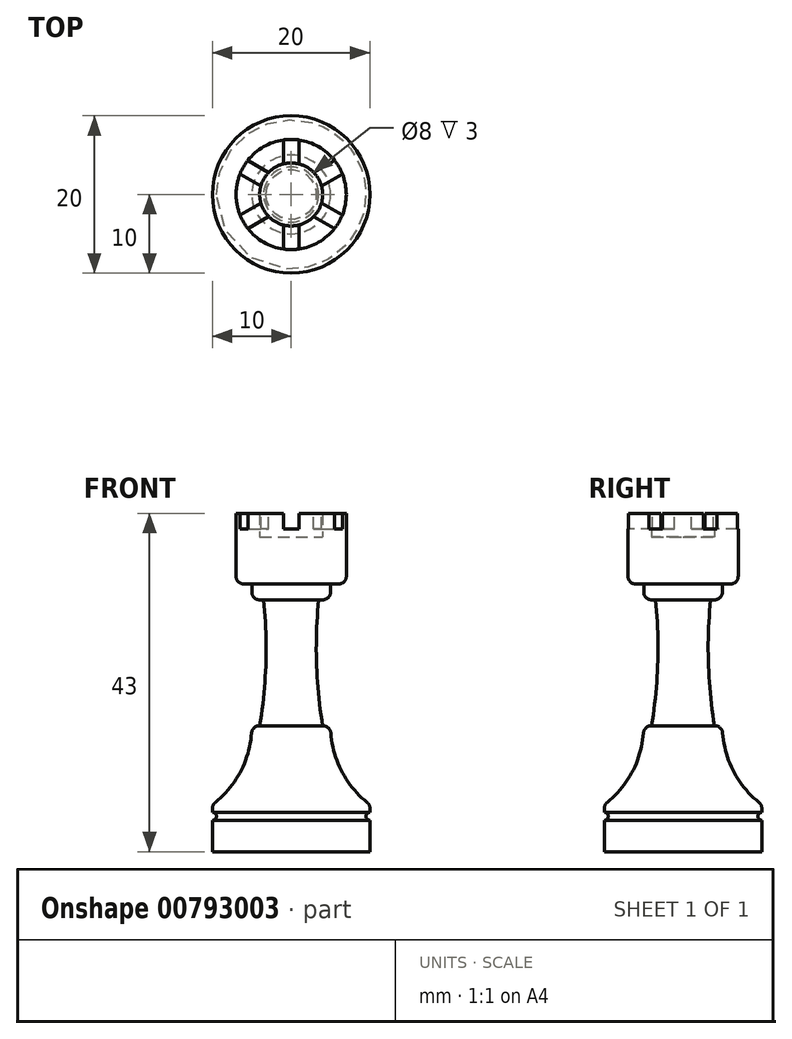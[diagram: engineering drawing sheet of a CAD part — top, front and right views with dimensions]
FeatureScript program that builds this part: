
annotation { "Feature Type Name" : "Feature", "Feature Type Description" : "" }
export const myFeature = defineFeature(function(context is Context, id is Id, definition is map)
    precondition{}
    {
        {
            var Q0;
            Q0=qCreatedBy(makeId("Front.planeOp"),FACE);
            var sketch = newSketch(context, id + "F0", { "sketchPlane" : qUnion([Q0])});
            skLineSegment(sketch, "E0.top", {"start": v(-10, 0) * mm, "end": v(10, 0) * mm, "construction": true});
            skLineSegment(sketch, "E0.left", {"start": v(10, 43) * mm, "end": v(10, 0) * mm, "construction": true});
            skLineSegment(sketch, "E0.right", {"start": v(-10, 43) * mm, "end": v(-10, 0) * mm, "construction": true});
            skLineSegment(sketch, "E1", {"start": v(0, 0) * mm, "end": v(0, 4) * mm, "construction": true});
            skLineSegment(sketch, "E2", {"start": v(0, 4) * mm, "end": v(-10, 4) * mm, "construction": true});
            skLineSegment(sketch, "E3", {"start": v(0, 4) * mm, "end": v(0, 5) * mm, "construction": true});
            skLineSegment(sketch, "E4", {"start": v(0, 5) * mm, "end": v(-10, 5) * mm, "construction": true});
            skLineSegment(sketch, "E5", {"start": v(0, 5) * mm, "end": v(0, 6) * mm, "construction": true});
            skLineSegment(sketch, "E6", {"start": v(0, 6) * mm, "end": v(-10, 6) * mm, "construction": true});
            skLineSegment(sketch, "E7", {"start": v(-9, 5) * mm, "end": v(-9, 4) * mm, "construction": true});
            skLineSegment(sketch, "E8", {"start": v(0, 6) * mm, "end": v(0, 16) * mm, "construction": true});
            skLineSegment(sketch, "E9", {"start": v(0, 16) * mm, "end": v(-10, 16) * mm, "construction": true});
            skLineSegment(sketch, "E10", {"start": v(0, 16) * mm, "end": v(0, 32) * mm, "construction": true});
            skLineSegment(sketch, "E11", {"start": v(0, 32) * mm, "end": v(-10, 32) * mm, "construction": true});
            skLineSegment(sketch, "E12", {"start": v(0, 32) * mm, "end": v(0, 34) * mm, "construction": true});
            skLineSegment(sketch, "E13", {"start": v(0, 34) * mm, "end": v(-10, 34) * mm, "construction": true});
            skLineSegment(sketch, "E14", {"start": v(-5, 16) * mm, "end": v(-5, 6) * mm, "construction": true});
            skLineSegment(sketch, "E15", {"start": v(0, 0) * mm, "end": v(-10, 0) * mm});
            skLineSegment(sketch, "E16", {"start": v(-10, 4) * mm, "end": v(-10, 0) * mm});
            skArc(sketch, "E17", {"start": v(-10, 4) * mm, "mid": v(-9.5, 4.5) * mm, "end": v(-10, 5) * mm});
            skLineSegment(sketch, "E18", {"start": v(-10, 5) * mm, "end": v(-10, 6) * mm});
            skArc(sketch, "E19", {"start": v(-10, 6) * mm, "mid": v(-6.32, 10.4) * mm, "end": v(-5, 16) * mm});
            skLineSegment(sketch, "E20", {"start": v(-5, 16) * mm, "end": v(-4, 16) * mm});
            skPoint(sketch, "E21.snap10", {"position": v(0, 33) * mm});
            skLineSegment(sketch, "E22", {"start": v(0, 0) * mm, "end": v(0, 54.13) * mm, "construction": true});
            skLineSegment(sketch, "E23", {"start": v(0, 43) * mm, "end": v(0, 0) * mm});
            skLineSegment(sketch, "E24", {"start": v(-7, 43) * mm, "end": v(-7, 34) * mm, "construction": true});
            skLineSegment(sketch, "E25", {"start": v(-5, 34) * mm, "end": v(-5, 32) * mm, "construction": true});
            skLineSegment(sketch, "E26", {"start": v(-3.5, 32) * mm, "end": v(-4, 16) * mm, "construction": true});
            skArc(sketch, "E27", {"start": v(-4, 16) * mm, "mid": v(-3.21, 23.98) * mm, "end": v(-3.5, 32) * mm});
            skLineSegment(sketch, "E28", {"start": v(-3.5, 32) * mm, "end": v(-5, 32) * mm});
            skLineSegment(sketch, "E29", {"start": v(-5, 32) * mm, "end": v(-5, 34) * mm});
            skLineSegment(sketch, "E30", {"start": v(-5, 34) * mm, "end": v(-7, 34) * mm});
            skLineSegment(sketch, "E31", {"start": v(-7, 34) * mm, "end": v(-7, 43) * mm});
            skLineSegment(sketch, "E32", {"start": v(-4, 43) * mm, "end": v(-4, 34) * mm, "construction": true});
            skLineSegment(sketch, "E33", {"start": v(-4, 40) * mm, "end": v(0, 40) * mm});
            skLineSegment(sketch, "E34", {"start": v(-4, 40) * mm, "end": v(-4, 43) * mm});
            skLineSegment(sketch, "E35", {"start": v(-7, 43) * mm, "end": v(-4, 43) * mm});
            skSolve(sketch);
        }
        {
            var Q0;
            Q0=qSketchRegion(id+"F0",true);
            var Q1;
            Q1=sQuery(id+"F0.wireOp",EDGE,"E22");
            revolve(context, id + "F1", {"surfaceOperationType" : NewSurfaceOperationType.NEW, "entities" : qUnion([Q0]), "axis" : qUnion([Q1]), "revolveType" : RevolveType.FULL});
        }
        {
            var Q0;
            Q0=makeQuery(id+"F1.opRevolve","SWEPT_EDGE",EDGE,{"disambiguationData":[OSD([sQuery(id+"F0.wireOp",EDGE,"E18"),sQuery(id+"F0.wireOp",EDGE,"E19")])]});
            var Q1;
            Q1=makeQuery(id+"F1.opRevolve","SWEPT_EDGE",EDGE,{"disambiguationData":[OSD([sQuery(id+"F0.wireOp",EDGE,"E19"),sQuery(id+"F0.wireOp",EDGE,"E20")])]});
            fillet(context, id + "F2", {"entities" : qUnion([Q0, Q1]), "radius" : 1 * mm, "tangentPropagation" : true, "allowEdgeOverflow" : false});
        }
        {
            var Q0;
            Q0=makeQuery(id+"F1.opRevolve","SWEPT_EDGE",EDGE,{"disambiguationData":[OSD([sQuery(id+"F0.wireOp",EDGE,"E30"),sQuery(id+"F0.wireOp",EDGE,"E31")])]});
            var Q1;
            Q1=makeQuery(id+"F1.opRevolve","SWEPT_EDGE",EDGE,{"disambiguationData":[OSD([sQuery(id+"F0.wireOp",EDGE,"E28"),sQuery(id+"F0.wireOp",EDGE,"E29")])]});
            fillet(context, id + "F3", {"entities" : qUnion([Q0, Q1]), "radius" : 1 * mm, "tangentPropagation" : true, "allowEdgeOverflow" : false});
        }
        {
            var Q0;
            Q0=makeQuery(id+"F1.opRevolve","SWEPT_FACE",FACE,{"disambiguationData":[OSD([sQuery(id+"F0.wireOp",EDGE,"E35")])]});
            var sketch = newSketch(context, id + "F4", { "sketchPlane" : qUnion([Q0])});
            skLineSegment(sketch, "E36", {"start": v(0, 7) * mm, "end": v(0, 0) * mm, "construction": true});
            skLineSegment(sketch, "E37", {"start": v(-1, 0) * mm, "end": v(-1, 7.52) * mm, "construction": true});
            skLineSegment(sketch, "E38", {"start": v(-1, 7.52) * mm, "end": v(1, 7.52) * mm, "construction": true});
            skLineSegment(sketch, "E39", {"start": v(1, 7.52) * mm, "end": v(1, 0) * mm, "construction": true});
            skLineSegment(sketch, "E40", {"start": v(-1, 6.93) * mm, "end": v(-1, 3.87) * mm});
            skLineSegment(sketch, "E41", {"start": v(1, 6.93) * mm, "end": v(1, 3.87) * mm});
            skLineSegment(sketch, "E42.1.0", {"start": v(-0.5, -0.87) * mm, "end": v(-7, 2.9) * mm, "construction": true});
            skLineSegment(sketch, "E42.1.1", {"start": v(-6.06, 3.5) * mm, "end": v(0, 0) * mm, "construction": true});
            skLineSegment(sketch, "E42.1.2", {"start": v(-6, 4.62) * mm, "end": v(0.5, 0.87) * mm, "construction": true});
            skLineSegment(sketch, "E42.2.0", {"start": v(0.5, -0.87) * mm, "end": v(-6, -4.62) * mm, "construction": true});
            skLineSegment(sketch, "E42.2.1", {"start": v(-6.06, -3.5) * mm, "end": v(0, 0) * mm, "construction": true});
            skLineSegment(sketch, "E42.2.2", {"start": v(-7, -2.9) * mm, "end": v(-0.5, 0.87) * mm, "construction": true});
            skLineSegment(sketch, "E42.3.0", {"start": v(1, 0) * mm, "end": v(1, -7.52) * mm, "construction": true});
            skLineSegment(sketch, "E42.3.1", {"start": v(0, -7) * mm, "end": v(0, 0) * mm, "construction": true});
            skLineSegment(sketch, "E42.3.2", {"start": v(-1, -7.52) * mm, "end": v(-1, 0) * mm, "construction": true});
            skLineSegment(sketch, "E42.4.0", {"start": v(0.5, 0.87) * mm, "end": v(7, -2.9) * mm, "construction": true});
            skLineSegment(sketch, "E42.4.1", {"start": v(6.06, -3.5) * mm, "end": v(0, 0) * mm, "construction": true});
            skLineSegment(sketch, "E42.4.2", {"start": v(6, -4.62) * mm, "end": v(-0.5, -0.87) * mm, "construction": true});
            skLineSegment(sketch, "E42.5.0", {"start": v(-0.5, 0.87) * mm, "end": v(6, 4.62) * mm, "construction": true});
            skLineSegment(sketch, "E42.5.1", {"start": v(6.06, 3.5) * mm, "end": v(0, 0) * mm, "construction": true});
            skLineSegment(sketch, "E42.5.2", {"start": v(7, 2.9) * mm, "end": v(0.5, -0.87) * mm, "construction": true});
            skPoint(sketch, "E42.center", {"position": v(0, 0) * mm});
            skLineSegment(sketch, "E43", {"start": v(-5.5, 4.33) * mm, "end": v(-2.85, 2.8) * mm});
            skLineSegment(sketch, "E44", {"start": v(-6.5, 2.6) * mm, "end": v(-3.85, 1.07) * mm});
            skLineSegment(sketch, "E45", {"start": v(-6.5, -2.6) * mm, "end": v(-3.85, -1.07) * mm});
            skLineSegment(sketch, "E46", {"start": v(-5.5, -4.33) * mm, "end": v(-2.85, -2.8) * mm});
            skLineSegment(sketch, "E47", {"start": v(-1, -3.87) * mm, "end": v(-1, -6.93) * mm});
            skLineSegment(sketch, "E48", {"start": v(1, -3.87) * mm, "end": v(1, -6.93) * mm});
            skLineSegment(sketch, "E49", {"start": v(2.85, -2.8) * mm, "end": v(5.5, -4.33) * mm});
            skLineSegment(sketch, "E50", {"start": v(3.85, -1.07) * mm, "end": v(6.5, -2.6) * mm});
            skLineSegment(sketch, "E51", {"start": v(3.85, 1.07) * mm, "end": v(6.5, 2.6) * mm});
            skLineSegment(sketch, "E52", {"start": v(2.85, 2.8) * mm, "end": v(5.5, 4.33) * mm});
            skSolve(sketch);
        }
        {
            var Q0;
            Q0 = qSketchRegion(id + "F4", true);
            var Q1;
            {var subQ0=sQuery(id+"F4.wireOp",EDGE,"E40");Q1=makeQuery(id+"F4.imprint","IMPRINT",FACE,{"disambiguationData":[TD([[makeQuery(id+"F4.imprint","IMPRINT",EDGE,{"derivedFrom":subQ0}),1.0]])]});}
            extrude(context, id + "F5", {"entities" : qUnion([Q0, Q1]), "operationType" : NewBodyOperationType.REMOVE, "oppositeDirection" : true, "depth" : 2 * mm, "offsetDistance" : 25 * mm});
        }
        {
            var Q0;
            {var subQ0=sQuery(id+"F4.wireOp",EDGE,"E43");Q0=makeQuery(id+"F4.imprint","IMPRINT",FACE,{"disambiguationData":[TD([[makeQuery(id+"F4.imprint","IMPRINT",EDGE,{"derivedFrom":subQ0}),-1.0]])]});}
            var Q1;
            {var subQ0=sQuery(id+"F4.wireOp",EDGE,"E45");Q1=makeQuery(id+"F4.imprint","IMPRINT",FACE,{"disambiguationData":[TD([[makeQuery(id+"F4.imprint","IMPRINT",EDGE,{"derivedFrom":subQ0}),-1.0]])]});}
            var Q2;
            {var subQ0=sQuery(id+"F4.wireOp",EDGE,"E47");Q2=makeQuery(id+"F4.imprint","IMPRINT",FACE,{"disambiguationData":[TD([[makeQuery(id+"F4.imprint","IMPRINT",EDGE,{"derivedFrom":subQ0}),1.0]])]});}
            var Q3;
            {var subQ0=sQuery(id+"F4.wireOp",EDGE,"E49");Q3=makeQuery(id+"F4.imprint","IMPRINT",FACE,{"disambiguationData":[TD([[makeQuery(id+"F4.imprint","IMPRINT",EDGE,{"derivedFrom":subQ0}),1.0]])]});}
            var Q4;
            {var subQ0=sQuery(id+"F4.wireOp",EDGE,"E51");Q4=makeQuery(id+"F4.imprint","IMPRINT",FACE,{"disambiguationData":[TD([[makeQuery(id+"F4.imprint","IMPRINT",EDGE,{"derivedFrom":subQ0}),1.0]])]});}
            extrude(context, id + "F6", {"entities" : qUnion([Q0, Q1, Q2, Q3, Q4]), "operationType" : NewBodyOperationType.REMOVE, "oppositeDirection" : true, "depth" : 2 * mm, "offsetDistance" : 25 * mm});
        }
    });
